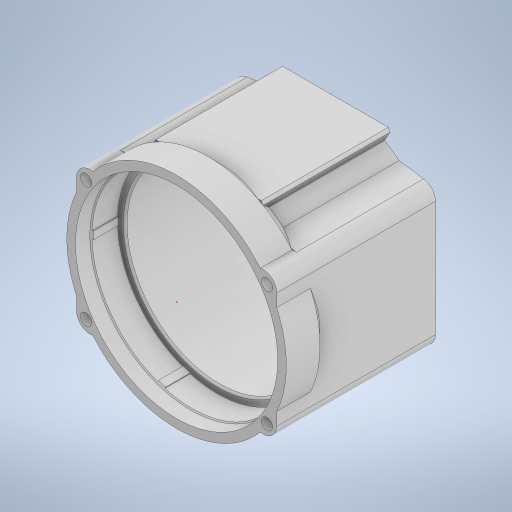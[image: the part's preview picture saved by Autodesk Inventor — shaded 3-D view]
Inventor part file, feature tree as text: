
AUTODESK INVENTOR PART (.ipt)
format: ipt  version: 2023.4 (Build 274418000, 418)  size: 751,104 bytes
history: native  units: mm
features: extrude x25, projected_geometry x19, sketch x15, chamfer x7, plane x2, mirror x1
ambient origin geometry x8: Origin, YZ Plane, XZ Plane, XY Plane, X Axis, Y Axis, Z Axis, Center Point
bodies: Solid1 (feature_tree)
feature tree (69):
  extrude  "Extrusion1"  Depth=3.0mm
  extrude  "Extrusion2"  Depth=45.0mm
  extrude  "Extrusion3"  Depth=14.0mm
  extrude  "Extrusion4"  Depth=50.0mm TaperAngle=0.0deg
  extrude  "Extrusion5"  Depth=11.5mm TaperAngle=0.0deg
  extrude  "Extrusion6"  Depth=21.0mm TaperAngle=0.0deg
  extrude  "Extrusion7"  Depth=5.0mm TaperAngle=0.0deg
  extrude  "Extrusion8"  Depth=30.0mm TaperAngle=0.0deg
  extrude  "Extrusion9"  Depth=30.0mm TaperAngle=0.0deg
  extrude  "Extrusion10"  Depth=10.0mm
  extrude  "Extrusion11"  Depth=10.0mm TaperAngle=0.0deg
  extrude  "Extrusion12"  Depth=10.0mm TaperAngle=0.0deg
  extrude  "Extrusion13"  Depth=10.0mm
  extrude  "Extrusion14"  Depth=10.0mm
  chamfer  "Chamfer5"  Distance=10.0mm
  chamfer  "Chamfer6"  Distance=14.0mm
  plane  "Work Plane2"
  extrude  "Extrusion17"  Depth=10.0mm TaperAngle=0.0deg
  chamfer  "Chamfer7"  Distance=5.75mm
  plane  "Work Plane3"
  extrude  "Extrusion18"  Depth=10.0mm
  extrude  "Extrusion25"  Depth=10.0mm TaperAngle=0.0deg
  mirror  "Mirror1"
  extrude  "Extrusion26"  Depth=10.0mm TaperAngle=45.0deg
  extrude  "Extrusion27"  Depth=10.0mm TaperAngle=45.0deg
  extrude  "Extrusion28"  Depth=10.0mm
  extrude  "Extrusion29"  Depth=10.0mm
  chamfer  "Chamfer8"  Distance=2.0mm
  extrude  "Extrusion30"  Depth=10.0mm TaperAngle=360.0deg
  chamfer  "Chamfer9"  Distance=13.0mm
  chamfer  "Chamfer10"  Distance=0.4mm Angle=45.0deg
  extrude  "Extrusion31"  Depth=10.0mm
  extrude  "Extrusion32"  Depth=10.0mm TaperAngle=0.0deg
  extrude  "Extrusion33"  TaperAngle=0.0deg  [1 undecoded]
  chamfer  "Chamfer11"  Distance=10.0mm
  sketch  "Sketch1"  dims[d0=96.0mm d1=3.0mm]
  sketch  "Sketch6"  dims[d2=108.166mm d3=45.0mm]
  projected_geometry  "Projected Loop1"
  projected_geometry  "Projected Loop2"
  projected_geometry  "Projected Loop3"
  projected_geometry  "Projected Loop4"
  sketch  "Sketch10"  dims[d4=30.0mm d5=14.0mm]
  projected_geometry  "Projected Loop5"
  projected_geometry  "Projected Loop6"
  sketch  "Sketch12"  dims[d6=91.7mm d7=50.0mm d8=0.0mm]
  projected_geometry  "Projected Loop7"
  sketch  "Sketch14"  dims[d9=114.0mm d10=11.5mm d11=0.0mm]
  sketch  "Sketch18"  dims[d12=103.9mm d13=21.0mm d14=0.0mm]
  sketch  "Sketch34"  dims[d15=128.0mm d16=5.0mm d17=0.0mm]
  sketch  "Sketch36"  dims[d18=3.0mm d19=30.0mm d20=0.0mm]
  projected_geometry  "Projected Loop12"
  projected_geometry  "Projected Loop13"
  sketch  "Sketch37"  dims[d22=44.0mm d23=30.0mm d24=0.0mm]
  projected_geometry  "Projected Loop14"
  projected_geometry  "Projected Loop15"
  sketch  "Sketch38"  dims[d25=10.0mm d26=0.0mm d27=2.0mm]
  projected_geometry  "Projected Loop16"
  projected_geometry  "Projected Loop17"
  sketch  "Sketch39"  dims[d28=2.0mm d29=10.0mm d30=0.0mm]
  projected_geometry  "Projected Loop18"
  sketch  "Sketch40"  dims[d31=10.0mm d32=0.0mm d33=11.5mm d34=0.0mm]
  projected_geometry  "Projected Loop19"
  projected_geometry  "Projected Loop20"
  projected_geometry  "Projected Loop21"
  projected_geometry  "Projected Loop22"
  sketch  "Sketch41"  dims[d35=10.0mm d36=0.0mm d37=113.0mm]
  sketch  "Sketch44"  dims[d38=5.75mm d39=5.75mm d40=10.0mm d41=0.0mm]
  sketch  "Sketch45"  dims[d51=14.0mm d52=14.0mm d53=2.0mm d54=0.0mm d58=5.75mm d59=5.75mm d60=16.0mm d61=0.0mm d62=2.0mm d63=2.0mm d64=45.0deg d65=2.0mm d66=2.0mm d67=45.0deg d85=0.4mm d86=4.0mm d87=2.0mm d88=50.0mm d90=360.0deg d92=13.0mm d93=0.0mm d94=0.4mm d95=2.0mm d96=45.0deg d97=105.0mm d98=13.0mm d99=0.0mm d136=0.0mm d137=0.0mm d144=10.0mm d145=0.0mm d146=10.0mm d147=0.0mm d148=10.0mm d149=0.0mm d150=30.0deg d151=30.0deg d152=10.0mm d153=0.0mm d154=2.0mm d155=2.0mm d156=45.0deg d157=10.0mm d158=0.0mm d159=5.0mm d160=2.0mm d161=45.0deg d162=5.999mm d163=2.0mm d164=45.0deg d165=10.0mm d166=0.0mm d167=66.0mm d168=0.0mm d169=4.8mm d170=0.0mm d173=1.0mm d174=2.0mm d175=45.0deg]
  projected_geometry  "Projected Loop24"
note: 1 required parameter value undecoded (feature->parameter linkage not recoverable at this tier; creation-order binding heuristic only, values carry confidence <= 0.55)
